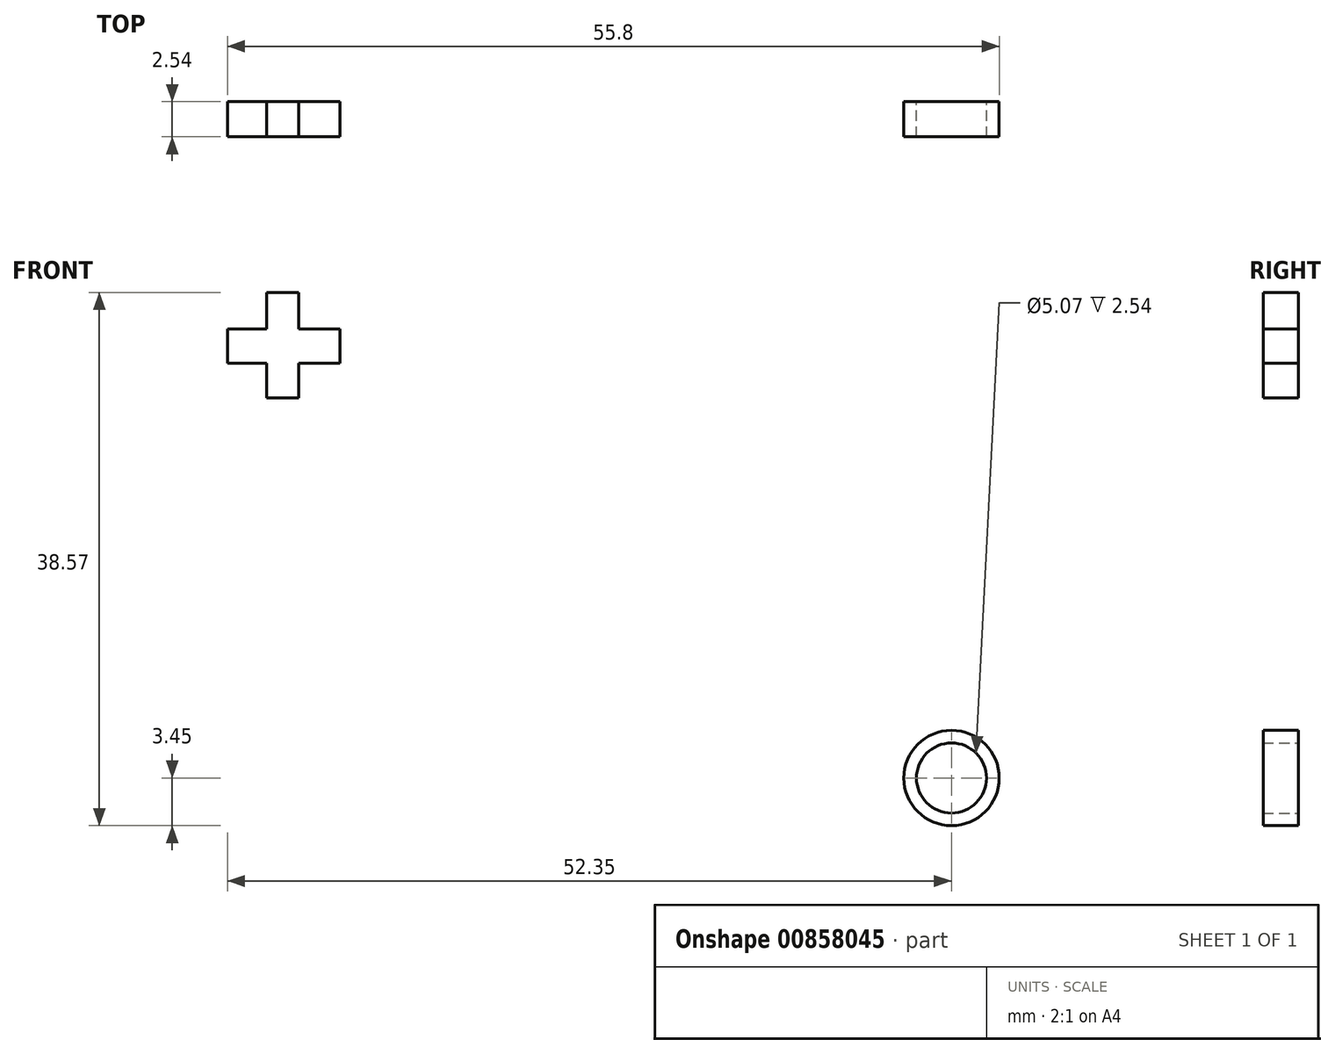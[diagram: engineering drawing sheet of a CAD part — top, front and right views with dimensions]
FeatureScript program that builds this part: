
annotation { "Feature Type Name" : "Feature", "Feature Type Description" : "" }
export const myFeature = defineFeature(function(context is Context, id is Id, definition is map)
    precondition{}
    {
        {
            var Q0;
            Q0=qCreatedBy(makeId("Front.planeOp"),FACE);
            var sketch = newSketch(context, id + "F0", { "sketchPlane" : qUnion([Q0])});
            skCircle(sketch, "E0", {"center": v(0, 0) * mm, "radius": 3.45 * mm});
            skSolve(sketch);
        }
        {
            var Q0;
            Q0=qSketchRegion(id+"F0",true);
            extrude(context, id + "F1", {"entities" : qUnion([Q0]), "depth" : 2.54 * mm});
        }
        {
            var Q0;
            Q0=qCreatedBy(makeId("Front.planeOp"),FACE);
            var sketch = newSketch(context, id + "F2", { "sketchPlane" : qUnion([Q0])});
            skCircle(sketch, "E1", {"center": v(0, 0) * mm, "radius": 2.53 * mm});
            skSolve(sketch);
        }
        {
            var Q0;
            Q0=makeQuery(id+"F2.imprint","IMPRINT",FACE,{"disambiguationData":[TD([[makeQuery(id+"F2.imprint","IMPRINT",EDGE,{"derivedFrom":sQuery(id+"F2.wireOp",EDGE,"E1")}),1.0]])]});
            extrude(context, id + "F3", {"entities" : qUnion([Q0]), "operationType" : NewBodyOperationType.REMOVE, "depth" : 25.15 * mm});
        }
        {
            var Q0;
            Q0=qCreatedBy(makeId("Front.planeOp"),FACE);
            var sketch = newSketch(context, id + "F4", { "sketchPlane" : qUnion([Q0])});
            skLineSegment(sketch, "E2.bottom", {"start": v(-52.35, 32.47) * mm, "end": v(-44.4, 32.47) * mm});
            skLineSegment(sketch, "E2.top", {"start": v(-52.35, 31.3) * mm, "end": v(-44.4, 31.3) * mm});
            skLineSegment(sketch, "E2.left", {"start": v(-52.35, 32.47) * mm, "end": v(-52.35, 31.3) * mm});
            skLineSegment(sketch, "E2.right", {"start": v(-44.4, 32.47) * mm, "end": v(-44.4, 31.3) * mm});
            skLineSegment(sketch, "E3.bottom", {"start": v(-47.21, 27.5) * mm, "end": v(-49.53, 27.5) * mm});
            skLineSegment(sketch, "E3.top", {"start": v(-47.21, 35.12) * mm, "end": v(-49.53, 35.12) * mm});
            skLineSegment(sketch, "E3.left", {"start": v(-47.21, 27.5) * mm, "end": v(-47.21, 35.12) * mm});
            skLineSegment(sketch, "E3.right", {"start": v(-49.53, 27.5) * mm, "end": v(-49.53, 35.12) * mm});
            skPoint(sketch, "E3.middle", {"position": v(-48.37, 31.3) * mm});
            skLineSegment(sketch, "E4.bottom", {"start": v(-52.35, 32.47) * mm, "end": v(-44.23, 32.47) * mm});
            skLineSegment(sketch, "E4.top", {"start": v(-52.35, 29.98) * mm, "end": v(-44.23, 29.98) * mm});
            skLineSegment(sketch, "E4.left", {"start": v(-52.35, 32.47) * mm, "end": v(-52.35, 29.98) * mm});
            skLineSegment(sketch, "E4.right", {"start": v(-44.23, 32.47) * mm, "end": v(-44.23, 29.98) * mm});
            skSolve(sketch);
        }
        {
            var Q0;
            Q0=qSketchRegion(id+"F4",true);
            extrude(context, id + "F5", {"entities" : qUnion([Q0]), "depth" : 2.54 * mm});
        }
    });
